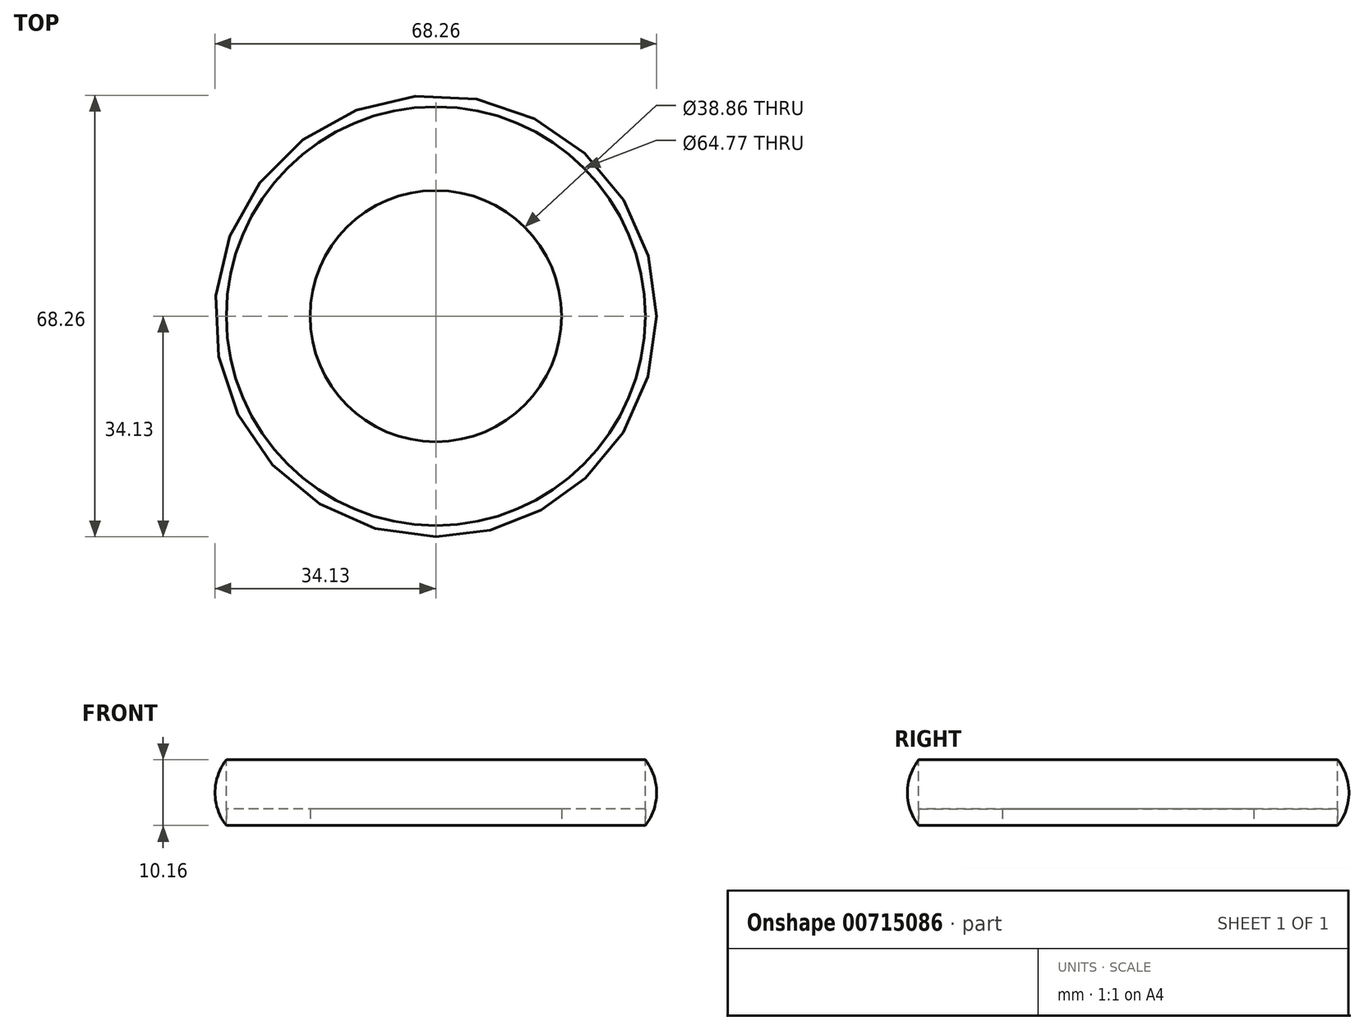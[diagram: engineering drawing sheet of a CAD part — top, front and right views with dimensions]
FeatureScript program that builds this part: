
annotation { "Feature Type Name" : "Feature", "Feature Type Description" : "" }
export const myFeature = defineFeature(function(context is Context, id is Id, definition is map)
    precondition{}
    {
        {
            var Q0;
            Q0=qCreatedBy(makeId("Top.planeOp"),FACE);
            var sketch = newSketch(context, id + "F0", { "sketchPlane" : qUnion([Q0])});
            skCircle(sketch, "E0", {"center": v(0, 0) * mm, "radius": 32.39 * mm});
            skCircle(sketch, "E1", {"center": v(0, 0) * mm, "radius": 31.62 * mm});
            skCircle(sketch, "E2", {"center": v(0, 0) * mm, "radius": 19.43 * mm});
            skSolve(sketch);
        }
        {
            var Q0;
            Q0=qCreatedBy(makeId("Front.planeOp"),FACE);
            var sketch = newSketch(context, id + "F1", { "sketchPlane" : qUnion([Q0])});
            skLineSegment(sketch, "E3", {"start": v(0, 0) * mm, "end": v(0, 158.75) * mm});
            skLineSegment(sketch, "E4", {"start": v(0, 158.75) * mm, "end": v(-19.05, 158.75) * mm});
            skLineSegment(sketch, "E5", {"start": v(0, 158.75) * mm, "end": v(19.05, 158.75) * mm});
            skPoint(sketch, "E6", {"position": v(0, 79.38) * mm});
            skLineSegment(sketch, "E7", {"start": v(0, 79.38) * mm, "end": v(0, 158.75) * mm});
            skPoint(sketch, "E8", {"position": v(0, 119.06) * mm});
            skLineSegment(sketch, "E9", {"start": v(0, 79.38) * mm, "end": v(0, 0) * mm});
            skPoint(sketch, "E10", {"position": v(0, 39.69) * mm});
            skLineSegment(sketch, "E11", {"start": v(0, 158.75) * mm, "end": v(0, 119.06) * mm});
            skLineSegment(sketch, "E12", {"start": v(0, 79.38) * mm, "end": v(0, 119.06) * mm});
            skLineSegment(sketch, "E13", {"start": v(0, 79.38) * mm, "end": v(0, 39.69) * mm});
            skLineSegment(sketch, "E14", {"start": v(0, 0) * mm, "end": v(0, 39.69) * mm});
            skPoint(sketch, "E15", {"position": v(0, 138.9) * mm});
            skPoint(sketch, "E16", {"position": v(0, 99.22) * mm});
            skPoint(sketch, "E17", {"position": v(0, 59.53) * mm});
            skPoint(sketch, "E18", {"position": v(0, 19.84) * mm});
            skLineSegment(sketch, "E19", {"start": v(0, 138.9) * mm, "end": v(-10.16, 138.9) * mm});
            skLineSegment(sketch, "E20", {"start": v(0, 119.06) * mm, "end": v(-19.05, 119.06) * mm});
            skLineSegment(sketch, "E21", {"start": v(0, 99.22) * mm, "end": v(-10.16, 99.22) * mm});
            skLineSegment(sketch, "E22", {"start": v(0, 79.38) * mm, "end": v(-19.05, 79.38) * mm});
            skLineSegment(sketch, "E23", {"start": v(0, 59.53) * mm, "end": v(-10.16, 59.53) * mm});
            skLineSegment(sketch, "E24", {"start": v(0, 39.69) * mm, "end": v(-19.05, 39.69) * mm});
            skFitSpline(sketch, "E25", {"points": [v(-19.05, 158.75) * mm, v(-10.16, 138.9) * mm, v(-19.05, 119.06) * mm, v(-10.16, 99.22) * mm, v(-19.05, 79.38) * mm, v(-10.16, 59.53) * mm, v(-19.05, 39.69) * mm, v(-19.05, 0) * mm], "startDerivative": vector(113.14, -145.9) * mm, "endDerivative": vector(34.46, -237.3) * mm});
            skLineSegment(sketch, "E26", {"start": v(-19.05, 0) * mm, "end": v(0, 0) * mm});
            skLineSegment(sketch, "E27", {"start": v(0, 0) * mm, "end": v(0, 172.98) * mm});
            skSolve(sketch);
        }
        {
            var Q0;
            Q0=qCreatedBy(makeId("Right.planeOp"),FACE);
            var sketch = newSketch(context, id + "F2", { "sketchPlane" : qUnion([Q0])});
            skLineSegment(sketch, "E28", {"start": v(0, 0) * mm, "end": v(-32.38, 0) * mm});
            skLineSegment(sketch, "E29", {"start": v(-32.38, 0) * mm, "end": v(-32.38, 10.16) * mm});
            skArc(sketch, "E30", {"start": v(-32.38, 10.16) * mm, "mid": v(-34.13, 5.08) * mm, "end": v(-32.39, 0) * mm});
            skSolve(sketch);
        }
        {
            var Q0;
            Q0=makeQuery(id+"F2.imprint","IMPRINT",FACE,{"disambiguationData":[TD([[makeQuery(id+"F2.imprint","IMPRINT",EDGE,{"derivedFrom":sQuery(id+"F2.wireOp",EDGE,"E29")}),1.0]])]});
            var Q1;
            Q1=sQuery(id+"F0.wireOp",EDGE,"E0");
            sweep(context, id + "F3", {"profiles" : qUnion([Q0]), "path" : qUnion([Q1])});
        }
        {
            var Q0;
            Q0=makeQuery(id+"F0.imprint","IMPRINT",FACE,{"disambiguationData":[TD([[makeQuery(id+"F0.imprint","IMPRINT",EDGE,{"derivedFrom":sQuery(id+"F0.wireOp",EDGE,"E0")}),1.0]])]});
            var Q1;
            Q1=makeQuery(id+"F0.imprint","IMPRINT",FACE,{"disambiguationData":[TD([[makeQuery(id+"F0.imprint","IMPRINT",EDGE,{"derivedFrom":sQuery(id+"F0.wireOp",EDGE,"E1")}),1.0]])]});
            extrude(context, id + "F4", {"entities" : qUnion([Q0, Q1]), "depth" : 2.54 * mm, "offsetDistance" : 25.4 * mm});
        }
    });
